# Revit family: rba-bim-rba4157-777-004
name_source: partatom
category: Plumbing Fixtures
revit_build: Autodesk Revit 2016 (Build: 20151007_0715(x64)
units: mm (PartAtom-declared; Revit-internal decimal feet)

## family parameters
Always vertical = Yes
Cut with Voids When Loaded = No
Part Type = Normal
Room Calculation Point = No
Round Connector Dimension = Use Diameter
Shared = No
Work Plane-Based = No

## types (1)
- RBA4157-777-004
    Accessible Compliant = AS1428.1-2009 Compliant
    Description = Phenolic Folding Shower Seat
    Manufacturer = Bobrick
    Materials and Finishes = #304 Satin Stainless Steel Frame with Black Phenolic Seat
    Model = RBA4157-777-004
    Modified Issue = 20200108.01
    Offset = 475 mm  [stored 1.5584 ft]
    URL = http://www.rba.com.au

note: [stored X ft] marks values corroborated as IEEE doubles in the binary element streams (Revit-internal decimal feet)

## geometry (parser evidence)
native form markers: Blend x16, Sweep x3
no freeform markers — native parametric forms only
